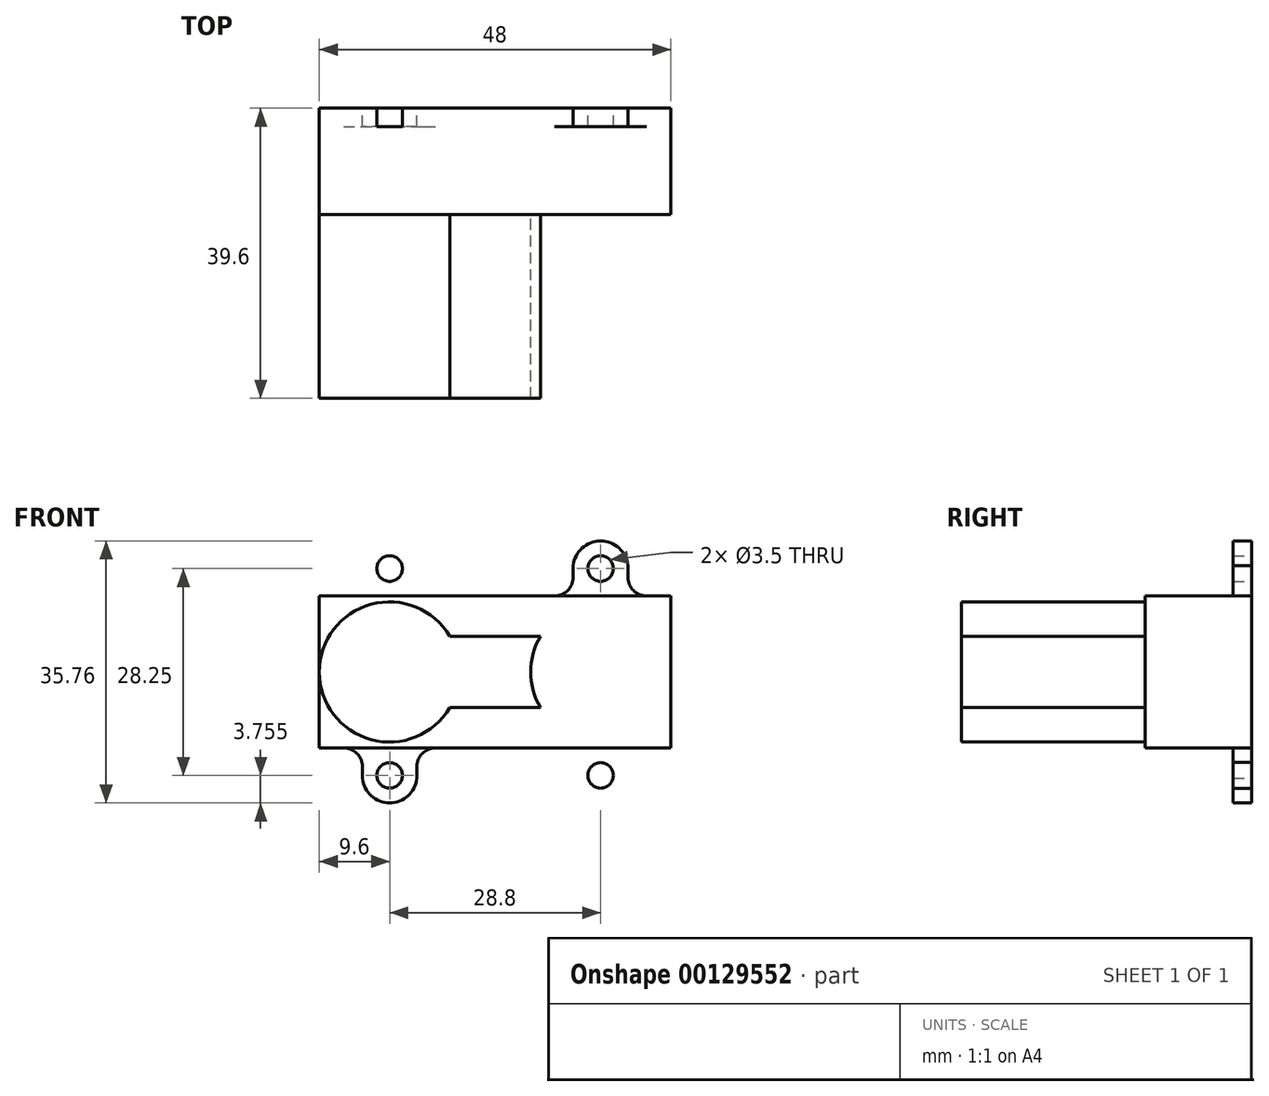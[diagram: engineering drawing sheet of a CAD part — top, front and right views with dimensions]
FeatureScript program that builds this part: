
annotation { "Feature Type Name" : "Feature", "Feature Type Description" : "" }
export const myFeature = defineFeature(function(context is Context, id is Id, definition is map)
    precondition{}
    {
        {
            var Q0;
            Q0=qCreatedBy(makeId("Front.planeOp"),FACE);
            var sketch = newSketch(context, id + "F0", { "sketchPlane" : qUnion([Q0])});
            skLineSegment(sketch, "E0.bottom", {"start": v(-24, 10.37) * mm, "end": v(24, 10.37) * mm});
            skLineSegment(sketch, "E0.top", {"start": v(-24, -10.37) * mm, "end": v(24, -10.37) * mm});
            skLineSegment(sketch, "E0.left", {"start": v(-24, 10.37) * mm, "end": v(-24, -10.37) * mm});
            skLineSegment(sketch, "E0.right", {"start": v(24, 10.37) * mm, "end": v(24, -10.37) * mm});
            skPoint(sketch, "E0.middle", {"position": v(0, 0) * mm});
            skSolve(sketch);
        }
        {
            var Q0;
            Q0=makeQuery(id+"F0.imprint","IMPRINT",FACE,{"disambiguationData":[TD([[makeQuery(id+"F0.imprint","IMPRINT",EDGE,{"derivedFrom":sQuery(id+"F0.wireOp",EDGE,"E0.bottom")}),-1.0]])]});
            extrude(context, id + "F1", {"entities" : qUnion([Q0]), "depth" : 14.5 * mm});
        }
        {
            var Q0;
            Q0=makeQuery(id+"F1.opExtrude","CAP_FACE",FACE,{"disambiguationData":[OSD([sQuery(id+"F0.wireOp",EDGE,"E0.bottom"),sQuery(id+"F0.wireOp",EDGE,"E0.top"),sQuery(id+"F0.wireOp",EDGE,"E0.left"),sQuery(id+"F0.wireOp",EDGE,"E0.right")])],"isStart":false});
            var sketch = newSketch(context, id + "F2", { "sketchPlane" : qUnion([Q0])});
            skLineSegment(sketch, "E1", {"start": v(0, 10.37) * mm, "end": v(0, -10.37) * mm, "construction": true});
            skCircle(sketch, "E2", {"center": v(-14.43, 0) * mm, "radius": 9.57 * mm});
            skLineSegment(sketch, "E3.bottom", {"start": v(-6.18, 4.88) * mm, "end": v(0, 4.88) * mm});
            skLineSegment(sketch, "E3.top", {"start": v(-6.18, -4.87) * mm, "end": v(0, -4.88) * mm});
            skPoint(sketch, "E3.middle", {"position": v(0, 0) * mm});
            skLineSegment(sketch, "E4.MirrorCS", {"start": v(6.18, 4.87) * mm, "end": v(0, 4.88) * mm});
            skLineSegment(sketch, "E5.MirrorCS", {"start": v(6.18, -4.88) * mm, "end": v(0, -4.88) * mm});
            skCircle(sketch, "E6.MirrorC", {"center": v(14.43, 0) * mm, "radius": 9.57 * mm});
            skSolve(sketch);
        }
        {
            var Q0;
            {var subQ0=sQuery(id+"F2.wireOp",EDGE,"E2");var subQ1=makeQuery(id+"F2.imprint","INTERSECT",VERTEX,{"derivedFrom":[subQ0,sQuery(id+"F2.wireOp",EDGE,"E3.bottom")]});Q0=makeQuery(id+"F2.imprint","IMPRINT",FACE,{"disambiguationData":[TD([[makeQuery(id+"F2.imprint","IMPRINT",EDGE,{"disambiguationData":[TD([[subQ1,-1.0]])],"derivedFrom":subQ0}),1.0]])]});}
            var Q1;
            {var subQ0=sQuery(id+"F2.wireOp",EDGE,"E6.MirrorC");var subQ1=makeQuery(id+"F2.imprint","INTERSECT",VERTEX,{"derivedFrom":[sQuery(id+"F2.wireOp",EDGE,"E4.MirrorCS"),subQ0]});Q1=makeQuery(id+"F2.imprint","IMPRINT",FACE,{"disambiguationData":[TD([[makeQuery(id+"F2.imprint","IMPRINT",EDGE,{"disambiguationData":[TD([[subQ1,-1.0]])],"derivedFrom":subQ0}),-1.0]])]});}
            extrude(context, id + "F3", {"entities" : qUnion([Q0, Q1]), "operationType" : NewBodyOperationType.ADD, "depth" : 25.1 * mm});
        }
        {
            var Q0;
            {var subQ2=sQuery(id+"F2.wireOp",EDGE,"E3.bottom");Q0=makeQuery(id+"F2.imprint","IMPRINT",FACE,{"disambiguationData":[TD([[makeQuery(id+"F2.imprint","IMPRINT",EDGE,{"derivedFrom":subQ2}),-1.0]])]});}
            extrude(context, id + "F4", {"entities" : qUnion([Q0]), "operationType" : NewBodyOperationType.ADD, "depth" : 22.25 * mm});
        }
        {
            var Q0;
            Q0=makeQuery(id+"F1.opExtrude","CAP_FACE",FACE,{"disambiguationData":[OSD([sQuery(id+"F0.wireOp",EDGE,"E0.bottom"),sQuery(id+"F0.wireOp",EDGE,"E0.top"),sQuery(id+"F0.wireOp",EDGE,"E0.left"),sQuery(id+"F0.wireOp",EDGE,"E0.right")])],"isStart":true});
            var sketch = newSketch(context, id + "F5", { "sketchPlane" : qUnion([Q0])});
            skCircle(sketch, "E7", {"center": v(-14.4, 14.12) * mm, "radius": 3.75 * mm});
            skCircle(sketch, "E8", {"center": v(-14.4, 14.12) * mm, "radius": 1.75 * mm});
            skLineSegment(sketch, "E9.bottom", {"start": v(-24, 10.37) * mm, "end": v(-20.67, 10.37) * mm});
            skLineSegment(sketch, "E9.top", {"start": v(-24, -10.37) * mm, "end": v(24, -10.37) * mm});
            skLineSegment(sketch, "E9.left", {"start": v(-24, 10.37) * mm, "end": v(-24, -10.37) * mm});
            skLineSegment(sketch, "E9.right", {"start": v(24, 10.37) * mm, "end": v(24, -10.37) * mm});
            skLineSegment(sketch, "E10", {"start": v(-18.13, 14.5) * mm, "end": v(-18.13, 12.91) * mm});
            skLineSegment(sketch, "E11", {"start": v(-10.67, 14.5) * mm, "end": v(-10.67, 12.91) * mm});
            skArc(sketch, "E12.filletArc", {"start": v(-20.67, 10.37) * mm, "mid": v(-18.87, 11.12) * mm, "end": v(-18.13, 12.91) * mm});
            skLineSegment(sketch, "E13", {"start": v(24, 10.37) * mm, "end": v(-8.13, 10.37) * mm});
            skPoint(sketch, "E14.visualSharp", {"position": v(-10.67, 10.37) * mm});
            skArc(sketch, "E14.filletArc", {"start": v(-10.67, 12.91) * mm, "mid": v(-9.93, 11.12) * mm, "end": v(-8.13, 10.37) * mm});
            skLineSegment(sketch, "E15.MirrorCS", {"start": v(10.67, 14.5) * mm, "end": v(10.67, 12.91) * mm});
            skLineSegment(sketch, "E16.MirrorCS", {"start": v(18.13, 14.5) * mm, "end": v(18.13, 12.91) * mm});
            skCircle(sketch, "E17.MirrorC", {"center": v(14.4, 14.12) * mm, "radius": 3.75 * mm});
            skCircle(sketch, "E18.MirrorC", {"center": v(14.4, 14.12) * mm, "radius": 1.75 * mm});
            skLineSegment(sketch, "E19.MirrorCS", {"start": v(24, 10.37) * mm, "end": v(20.67, 10.37) * mm});
            skPoint(sketch, "E20.MirrorP", {"position": v(10.67, 10.37) * mm});
            skArc(sketch, "E21.MirrorCS", {"start": v(10.67, 12.91) * mm, "mid": v(9.93, 11.12) * mm, "end": v(8.13, 10.37) * mm});
            skArc(sketch, "E22.MirrorCS", {"start": v(20.67, 10.37) * mm, "mid": v(18.87, 11.12) * mm, "end": v(18.13, 12.91) * mm});
            skLineSegment(sketch, "E23.MirrorCS", {"start": v(18.13, -14.5) * mm, "end": v(18.13, -12.91) * mm});
            skLineSegment(sketch, "E24.MirrorCS", {"start": v(10.67, -14.5) * mm, "end": v(10.67, -12.91) * mm});
            skLineSegment(sketch, "E25.MirrorCS", {"start": v(-18.13, -14.5) * mm, "end": v(-18.13, -12.91) * mm});
            skLineSegment(sketch, "E26.MirrorCS", {"start": v(-10.67, -14.5) * mm, "end": v(-10.67, -12.91) * mm});
            skLineSegment(sketch, "E27.MirrorCS", {"start": v(24, -10.37) * mm, "end": v(20.67, -10.37) * mm});
            skPoint(sketch, "E28.MirrorP", {"position": v(10.67, -10.37) * mm});
            skArc(sketch, "E29.MirrorCS", {"start": v(-10.67, -12.91) * mm, "mid": v(-9.93, -11.12) * mm, "end": v(-8.13, -10.37) * mm});
            skLineSegment(sketch, "E30.MirrorCS", {"start": v(24, -10.37) * mm, "end": v(-8.13, -10.37) * mm});
            skArc(sketch, "E31.MirrorCS", {"start": v(-20.67, -10.37) * mm, "mid": v(-18.87, -11.12) * mm, "end": v(-18.13, -12.91) * mm});
            skArc(sketch, "E32.MirrorCS", {"start": v(20.67, -10.37) * mm, "mid": v(18.87, -11.12) * mm, "end": v(18.13, -12.91) * mm});
            skLineSegment(sketch, "E33.MirrorCS", {"start": v(-24, -10.37) * mm, "end": v(-20.67, -10.37) * mm});
            skCircle(sketch, "E34.MirrorC", {"center": v(-14.4, -14.12) * mm, "radius": 1.75 * mm});
            skArc(sketch, "E35.MirrorCS", {"start": v(10.67, -12.91) * mm, "mid": v(9.93, -11.12) * mm, "end": v(8.13, -10.37) * mm});
            skCircle(sketch, "E36.MirrorC", {"center": v(14.4, -14.12) * mm, "radius": 3.75 * mm});
            skCircle(sketch, "E37.MirrorC", {"center": v(-14.4, -14.12) * mm, "radius": 3.75 * mm});
            skCircle(sketch, "E38.MirrorC", {"center": v(14.4, -14.12) * mm, "radius": 1.75 * mm});
            skPoint(sketch, "E39.MirrorP", {"position": v(-10.67, -10.37) * mm});
            skSolve(sketch);
        }
        {
            var Q0;
            {var subQ0=sQuery(id+"F5.wireOp",EDGE,"E10");var subQ1=sQuery(id+"F5.wireOp",EDGE,"E7");var subQ2=makeQuery(id+"F5.imprint","INTERSECT",VERTEX,{"disambiguationData":[OD(0.0)],"derivedFrom":[subQ1,subQ0]});Q0=makeQuery(id+"F5.imprint","IMPRINT",FACE,{"disambiguationData":[TD([[makeQuery(id+"F5.imprint","IMPRINT",EDGE,{"disambiguationData":[TD([[subQ2,-1.0]])],"derivedFrom":subQ1}),1.0]])]});}
            var Q1;
            {var subQ0=sQuery(id+"F5.wireOp",EDGE,"E11");var subQ1=sQuery(id+"F5.wireOp",EDGE,"E7");var subQ2=makeQuery(id+"F5.imprint","INTERSECT",VERTEX,{"disambiguationData":[OD(0.0)],"derivedFrom":[subQ1,subQ0]});Q1=makeQuery(id+"F5.imprint","IMPRINT",FACE,{"disambiguationData":[TD([[makeQuery(id+"F5.imprint","IMPRINT",EDGE,{"disambiguationData":[TD([[subQ2,1.0]])],"derivedFrom":subQ1}),1.0]])]});}
            var Q2;
            {var subQ0=sQuery(id+"F5.wireOp",EDGE,"E17.MirrorC");var subQ1=sQuery(id+"F5.wireOp",EDGE,"E15.MirrorCS");var subQ2=makeQuery(id+"F5.imprint","INTERSECT",VERTEX,{"disambiguationData":[OD(0.0)],"derivedFrom":[subQ1,subQ0]});Q2=makeQuery(id+"F5.imprint","IMPRINT",FACE,{"disambiguationData":[TD([[makeQuery(id+"F5.imprint","IMPRINT",EDGE,{"disambiguationData":[TD([[subQ2,-1.0]])],"derivedFrom":subQ1}),-1.0]])]});}
            var Q3;
            {var subQ0=sQuery(id+"F5.wireOp",EDGE,"E17.MirrorC");var subQ1=sQuery(id+"F5.wireOp",EDGE,"E16.MirrorCS");var subQ2=makeQuery(id+"F5.imprint","INTERSECT",VERTEX,{"disambiguationData":[OD(0.0)],"derivedFrom":[subQ1,subQ0]});Q3=makeQuery(id+"F5.imprint","IMPRINT",FACE,{"disambiguationData":[TD([[makeQuery(id+"F5.imprint","IMPRINT",EDGE,{"disambiguationData":[TD([[subQ2,-1.0]])],"derivedFrom":subQ1}),1.0]])]});}
            var Q4;
            {var subQ0=sQuery(id+"F5.wireOp",EDGE,"E36.MirrorC");var subQ1=sQuery(id+"F5.wireOp",EDGE,"E23.MirrorCS");var subQ2=makeQuery(id+"F5.imprint","INTERSECT",VERTEX,{"disambiguationData":[OD(0.0)],"derivedFrom":[subQ1,subQ0]});Q4=makeQuery(id+"F5.imprint","IMPRINT",FACE,{"disambiguationData":[TD([[makeQuery(id+"F5.imprint","IMPRINT",EDGE,{"disambiguationData":[TD([[subQ2,-1.0]])],"derivedFrom":subQ1}),-1.0]])]});}
            var Q5;
            {var subQ0=sQuery(id+"F5.wireOp",EDGE,"E36.MirrorC");var subQ1=sQuery(id+"F5.wireOp",EDGE,"E24.MirrorCS");var subQ2=makeQuery(id+"F5.imprint","INTERSECT",VERTEX,{"disambiguationData":[OD(0.0)],"derivedFrom":[subQ1,subQ0]});Q5=makeQuery(id+"F5.imprint","IMPRINT",FACE,{"disambiguationData":[TD([[makeQuery(id+"F5.imprint","IMPRINT",EDGE,{"disambiguationData":[TD([[subQ2,-1.0]])],"derivedFrom":subQ1}),1.0]])]});}
            var Q6;
            {var subQ0=sQuery(id+"F5.wireOp",EDGE,"E37.MirrorC");var subQ1=sQuery(id+"F5.wireOp",EDGE,"E25.MirrorCS");var subQ2=makeQuery(id+"F5.imprint","INTERSECT",VERTEX,{"disambiguationData":[OD(0.0)],"derivedFrom":[subQ1,subQ0]});Q6=makeQuery(id+"F5.imprint","IMPRINT",FACE,{"disambiguationData":[TD([[makeQuery(id+"F5.imprint","IMPRINT",EDGE,{"disambiguationData":[TD([[subQ2,-1.0]])],"derivedFrom":subQ1}),1.0]])]});}
            var Q7;
            {var subQ0=sQuery(id+"F5.wireOp",EDGE,"E37.MirrorC");var subQ1=sQuery(id+"F5.wireOp",EDGE,"E26.MirrorCS");var subQ2=makeQuery(id+"F5.imprint","INTERSECT",VERTEX,{"disambiguationData":[OD(0.0)],"derivedFrom":[subQ1,subQ0]});Q7=makeQuery(id+"F5.imprint","IMPRINT",FACE,{"disambiguationData":[TD([[makeQuery(id+"F5.imprint","IMPRINT",EDGE,{"disambiguationData":[TD([[subQ2,-1.0]])],"derivedFrom":subQ1}),-1.0]])]});}
            var Q8;
            {var subQ0=sQuery(id+"F5.wireOp",EDGE,"E29.MirrorCS");Q8=makeQuery(id+"F5.imprint","IMPRINT",FACE,{"disambiguationData":[TD([[makeQuery(id+"F5.imprint","IMPRINT",EDGE,{"derivedFrom":subQ0}),1.0]])]});}
            var Q9;
            {var subQ0=sQuery(id+"F5.wireOp",EDGE,"E31.MirrorCS");Q9=makeQuery(id+"F5.imprint","IMPRINT",FACE,{"disambiguationData":[TD([[makeQuery(id+"F5.imprint","IMPRINT",EDGE,{"derivedFrom":subQ0}),1.0]])]});}
            var Q10;
            {var subQ0=sQuery(id+"F5.wireOp",EDGE,"E22.MirrorCS");Q10=makeQuery(id+"F5.imprint","IMPRINT",FACE,{"disambiguationData":[TD([[makeQuery(id+"F5.imprint","IMPRINT",EDGE,{"derivedFrom":subQ0}),1.0]])]});}
            var Q11;
            {var subQ0=sQuery(id+"F5.wireOp",EDGE,"E21.MirrorCS");Q11=makeQuery(id+"F5.imprint","IMPRINT",FACE,{"disambiguationData":[TD([[makeQuery(id+"F5.imprint","IMPRINT",EDGE,{"derivedFrom":subQ0}),1.0]])]});}
            var Q12;
            {var subQ0=sQuery(id+"F5.wireOp",EDGE,"E32.MirrorCS");Q12=makeQuery(id+"F5.imprint","IMPRINT",FACE,{"disambiguationData":[TD([[makeQuery(id+"F5.imprint","IMPRINT",EDGE,{"derivedFrom":subQ0}),-1.0]])]});}
            var Q13;
            {var subQ0=sQuery(id+"F5.wireOp",EDGE,"E35.MirrorCS");Q13=makeQuery(id+"F5.imprint","IMPRINT",FACE,{"disambiguationData":[TD([[makeQuery(id+"F5.imprint","IMPRINT",EDGE,{"derivedFrom":subQ0}),-1.0]])]});}
            var Q14;
            Q14=makeQuery(id+"F5.imprint","IMPRINT",FACE,{"disambiguationData":[TD([[makeQuery(id+"F5.imprint","IMPRINT",EDGE,{"derivedFrom":sQuery(id+"F5.wireOp",EDGE,"E8")}),-1.0]])]});
            var Q15;
            Q15=makeQuery(id+"F5.imprint","IMPRINT",FACE,{"disambiguationData":[TD([[makeQuery(id+"F5.imprint","IMPRINT",EDGE,{"derivedFrom":sQuery(id+"F5.wireOp",EDGE,"E18.MirrorC")}),1.0]])]});
            var Q16;
            Q16=makeQuery(id+"F5.imprint","IMPRINT",FACE,{"disambiguationData":[TD([[makeQuery(id+"F5.imprint","IMPRINT",EDGE,{"derivedFrom":sQuery(id+"F5.wireOp",EDGE,"E38.MirrorC")}),-1.0]])]});
            var Q17;
            Q17=makeQuery(id+"F5.imprint","IMPRINT",FACE,{"disambiguationData":[TD([[makeQuery(id+"F5.imprint","IMPRINT",EDGE,{"derivedFrom":sQuery(id+"F5.wireOp",EDGE,"E34.MirrorC")}),1.0]])]});
            var Q18;
            {var subQ5=sQuery(id+"F5.wireOp",EDGE,"E12.filletArc");Q18=makeQuery(id+"F5.imprint","IMPRINT",FACE,{"disambiguationData":[TD([[makeQuery(id+"F5.imprint","IMPRINT",EDGE,{"derivedFrom":subQ5}),-1.0]])]});}
            var Q19;
            {var subQ5=sQuery(id+"F5.wireOp",EDGE,"E14.filletArc");Q19=makeQuery(id+"F5.imprint","IMPRINT",FACE,{"disambiguationData":[TD([[makeQuery(id+"F5.imprint","IMPRINT",EDGE,{"derivedFrom":subQ5}),-1.0]])]});}
            extrude(context, id + "F6", {"entities" : qUnion([Q0, Q1, Q2, Q3, Q4, Q5, Q6, Q7, Q8, Q9, Q10, Q11, Q12, Q13, Q14, Q15, Q16, Q17, Q18, Q19]), "operationType" : NewBodyOperationType.ADD, "oppositeDirection" : true, "depth" : 2.5 * mm});
        }
    });
